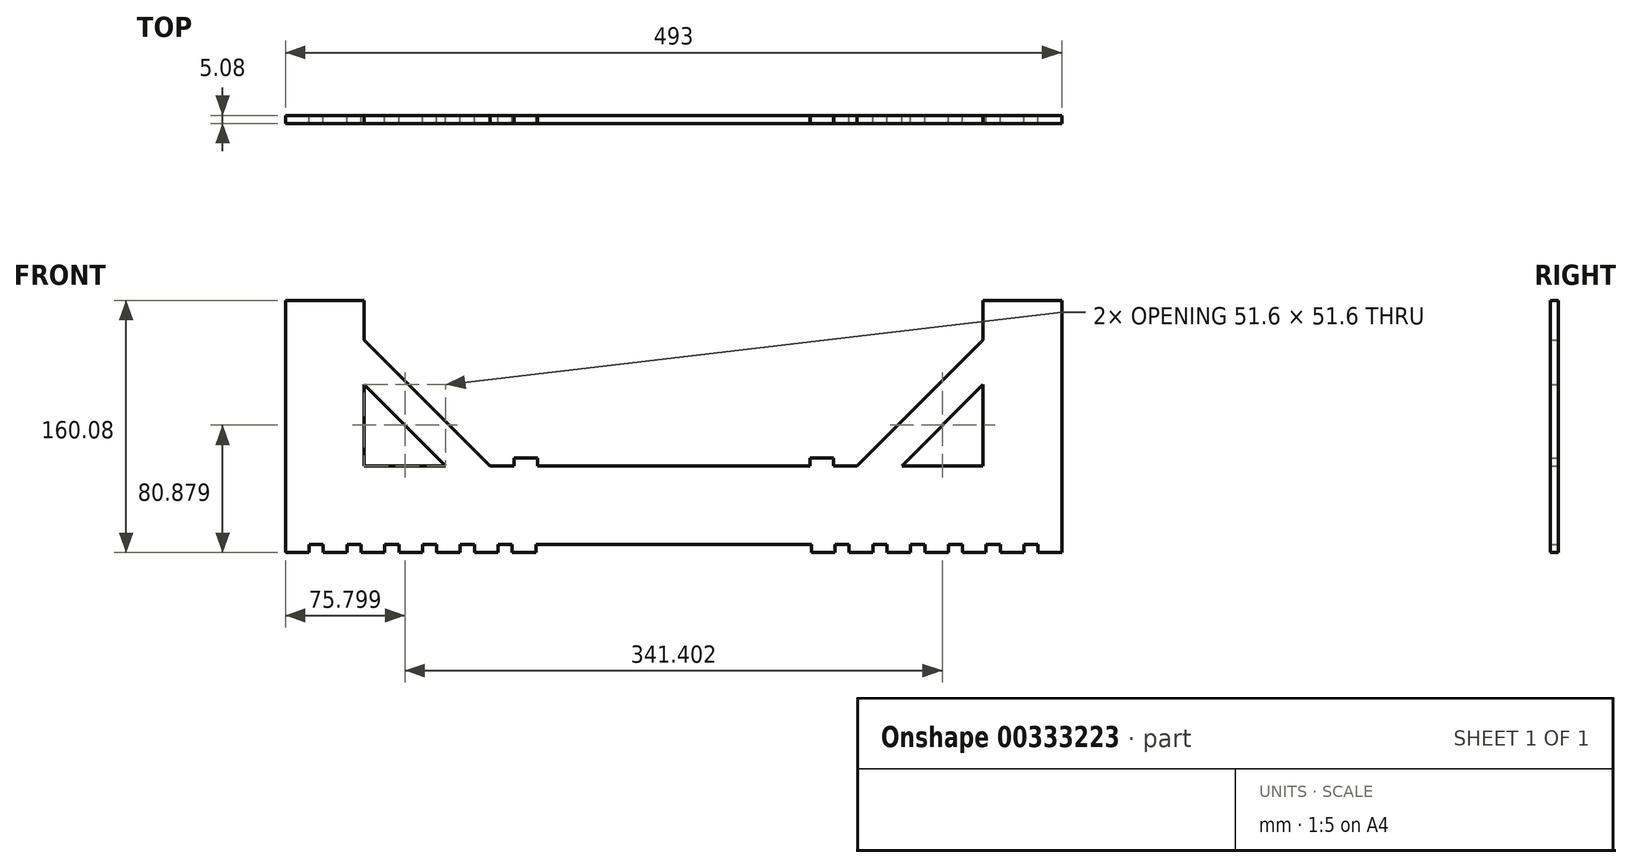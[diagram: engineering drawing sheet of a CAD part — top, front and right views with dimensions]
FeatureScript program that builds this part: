
annotation { "Feature Type Name" : "Feature", "Feature Type Description" : "" }
export const myFeature = defineFeature(function(context is Context, id is Id, definition is map)
    precondition{}
    {
        {
            var Q0;
            Q0=qCreatedBy(makeId("Front.planeOp"),FACE);
            var sketch = newSketch(context, id + "F0", { "sketchPlane" : qUnion([Q0])});
            skLineSegment(sketch, "E0", {"start": v(0, 0) * mm, "end": v(-246.5, 0) * mm});
            skLineSegment(sketch, "E1", {"start": v(-246.5, 0) * mm, "end": v(-246.5, 130) * mm});
            skLineSegment(sketch, "E2", {"start": v(-246.5, 130) * mm, "end": v(-196.5, 130) * mm});
            skLineSegment(sketch, "E3", {"start": v(-196.5, 130) * mm, "end": v(-196.5, 50) * mm});
            skLineSegment(sketch, "E4", {"start": v(-196.5, 50) * mm, "end": v(0, 50) * mm});
            skLineSegment(sketch, "E5", {"start": v(0, 50) * mm, "end": v(0, 0) * mm});
            skLineSegment(sketch, "E6", {"start": v(-196.5, 130) * mm, "end": v(-116.5, 50) * mm});
            skLineSegment(sketch, "E7", {"start": v(-196.5, 101.6) * mm, "end": v(-144.9, 50) * mm});
            skLineSegment(sketch, "E8", {"start": v(-246.5, 0) * mm, "end": v(-246.5, -5.08) * mm});
            skLineSegment(sketch, "E9", {"start": v(-246.5, -5.08) * mm, "end": v(-231.5, -5.08) * mm});
            skLineSegment(sketch, "E10", {"start": v(-231.5, -5.08) * mm, "end": v(-231.5, 0) * mm});
            skLineSegment(sketch, "E11.MirrorCS", {"start": v(196.5, 50) * mm, "end": v(0, 50) * mm});
            skLineSegment(sketch, "E12.MirrorCS", {"start": v(196.5, 130) * mm, "end": v(196.5, 50) * mm});
            skLineSegment(sketch, "E13.MirrorCS", {"start": v(196.5, 130) * mm, "end": v(116.5, 50) * mm});
            skLineSegment(sketch, "E14.MirrorCS", {"start": v(196.5, 101.6) * mm, "end": v(144.9, 50) * mm});
            skLineSegment(sketch, "E15.MirrorCS", {"start": v(246.5, 130) * mm, "end": v(196.5, 130) * mm});
            skLineSegment(sketch, "E16.MirrorCS", {"start": v(0, 0) * mm, "end": v(246.5, 0) * mm});
            skLineSegment(sketch, "E17.MirrorCS", {"start": v(246.5, 0) * mm, "end": v(246.5, 130) * mm});
            skLineSegment(sketch, "E18.1.0.0", {"start": v(-207.5, -5.08) * mm, "end": v(-207.5, 0) * mm});
            skLineSegment(sketch, "E18.1.0.1", {"start": v(-222.5, -5.08) * mm, "end": v(-207.5, -5.08) * mm});
            skLineSegment(sketch, "E18.1.0.2", {"start": v(-222.5, 0) * mm, "end": v(-222.5, -5.08) * mm});
            skLineSegment(sketch, "E18.2.0.0", {"start": v(-183.5, -5.08) * mm, "end": v(-183.5, 0) * mm});
            skLineSegment(sketch, "E18.2.0.1", {"start": v(-198.5, -5.08) * mm, "end": v(-183.5, -5.08) * mm});
            skLineSegment(sketch, "E18.2.0.2", {"start": v(-198.5, 0) * mm, "end": v(-198.5, -5.08) * mm});
            skLineSegment(sketch, "E18.3.0.0", {"start": v(-159.5, -5.08) * mm, "end": v(-159.5, 0) * mm});
            skLineSegment(sketch, "E18.3.0.1", {"start": v(-174.5, -5.08) * mm, "end": v(-159.5, -5.08) * mm});
            skLineSegment(sketch, "E18.3.0.2", {"start": v(-174.5, 0) * mm, "end": v(-174.5, -5.08) * mm});
            skLineSegment(sketch, "E18.4.0.0", {"start": v(-135.5, -5.08) * mm, "end": v(-135.5, 0) * mm});
            skLineSegment(sketch, "E18.4.0.1", {"start": v(-150.5, -5.08) * mm, "end": v(-135.5, -5.08) * mm});
            skLineSegment(sketch, "E18.4.0.2", {"start": v(-150.5, 0) * mm, "end": v(-150.5, -5.08) * mm});
            skLineSegment(sketch, "E18.5.0.0", {"start": v(-111.5, -5.08) * mm, "end": v(-111.5, 0) * mm});
            skLineSegment(sketch, "E18.5.0.1", {"start": v(-126.5, -5.08) * mm, "end": v(-111.5, -5.08) * mm});
            skLineSegment(sketch, "E18.5.0.2", {"start": v(-126.5, 0) * mm, "end": v(-126.5, -5.08) * mm});
            skLineSegment(sketch, "E18.6.0.0", {"start": v(-87.5, -5.08) * mm, "end": v(-87.5, 0) * mm});
            skLineSegment(sketch, "E18.6.0.1", {"start": v(-102.5, -5.08) * mm, "end": v(-87.5, -5.08) * mm});
            skLineSegment(sketch, "E18.6.0.2", {"start": v(-102.5, 0) * mm, "end": v(-102.5, -5.08) * mm});
            skLineSegment(sketch, "E18.direction1", {"start": v(-246.5, -5.08) * mm, "end": v(-222.5, -5.08) * mm, "construction": true});
            skLineSegment(sketch, "E19.MirrorCS", {"start": v(246.5, 0) * mm, "end": v(246.5, -5.08) * mm});
            skLineSegment(sketch, "E20.MirrorCS", {"start": v(231.5, -5.08) * mm, "end": v(231.5, 0) * mm});
            skLineSegment(sketch, "E21.MirrorCS", {"start": v(222.5, 0) * mm, "end": v(222.5, -5.08) * mm});
            skLineSegment(sketch, "E22.MirrorCS", {"start": v(222.5, -5.08) * mm, "end": v(207.5, -5.08) * mm});
            skLineSegment(sketch, "E23.MirrorCS", {"start": v(207.5, -5.08) * mm, "end": v(207.5, 0) * mm});
            skLineSegment(sketch, "E24.MirrorCS", {"start": v(198.5, 0) * mm, "end": v(198.5, -5.08) * mm});
            skLineSegment(sketch, "E25.MirrorCS", {"start": v(198.5, -5.08) * mm, "end": v(183.5, -5.08) * mm});
            skLineSegment(sketch, "E26.MirrorCS", {"start": v(183.5, -5.08) * mm, "end": v(183.5, 0) * mm});
            skLineSegment(sketch, "E27.MirrorCS", {"start": v(174.5, 0) * mm, "end": v(174.5, -5.08) * mm});
            skLineSegment(sketch, "E28.MirrorCS", {"start": v(174.5, -5.08) * mm, "end": v(159.5, -5.08) * mm});
            skLineSegment(sketch, "E29.MirrorCS", {"start": v(159.5, -5.08) * mm, "end": v(159.5, 0) * mm});
            skLineSegment(sketch, "E30.MirrorCS", {"start": v(150.5, 0) * mm, "end": v(150.5, -5.08) * mm});
            skLineSegment(sketch, "E31.MirrorCS", {"start": v(150.5, -5.08) * mm, "end": v(135.5, -5.08) * mm});
            skLineSegment(sketch, "E32.MirrorCS", {"start": v(135.5, -5.08) * mm, "end": v(135.5, 0) * mm});
            skLineSegment(sketch, "E33.MirrorCS", {"start": v(87.5, -5.08) * mm, "end": v(87.5, 0) * mm});
            skLineSegment(sketch, "E34.MirrorCS", {"start": v(102.5, -5.08) * mm, "end": v(87.5, -5.08) * mm});
            skLineSegment(sketch, "E35.MirrorCS", {"start": v(102.5, 0) * mm, "end": v(102.5, -5.08) * mm});
            skLineSegment(sketch, "E36.MirrorCS", {"start": v(111.5, -5.08) * mm, "end": v(111.5, 0) * mm});
            skLineSegment(sketch, "E37.MirrorCS", {"start": v(126.5, 0) * mm, "end": v(126.5, -5.08) * mm});
            skLineSegment(sketch, "E38.MirrorCS", {"start": v(126.5, -5.08) * mm, "end": v(111.5, -5.08) * mm});
            skLineSegment(sketch, "E39", {"start": v(231.5, -5.08) * mm, "end": v(246.5, -5.08) * mm});
            skSolve(sketch);
        }
        {
            var Q0;
            Q0=qSketchRegion(id+"F0",true);
            extrude(context, id + "F1", {"entities" : qUnion([Q0]), "depth" : 5.08 * mm});
        }
        {
            var Q0;
            Q0=makeQuery(id+"F1.opExtrude","SWEPT_FACE",FACE,{"disambiguationData":[OSD([sQuery(id+"F0.wireOp",EDGE,"E2")])]});
            var Q1;
            Q1=makeQuery(id+"F1.opExtrude","SWEPT_FACE",FACE,{"disambiguationData":[OSD([sQuery(id+"F0.wireOp",EDGE,"E15.MirrorCS")])]});
            extrude(context, id + "F2", {"entities" : qUnion([Q0, Q1]), "operationType" : NewBodyOperationType.ADD, "depth" : 25 * mm});
        }
        {
            var Q0;
            Q0=makeQuery(id+"F1.opExtrude","SWEPT_FACE",FACE,{"disambiguationData":[OSD([sQuery(id+"F0.wireOp",EDGE,"E4"),sQuery(id+"F0.wireOp",EDGE,"E11.MirrorCS")])]});
            var sketch = newSketch(context, id + "F3", { "sketchPlane" : qUnion([Q0])});
            skLineSegment(sketch, "E40.bottom", {"start": v(101.5, -5.08) * mm, "end": v(86.5, -5.08) * mm});
            skLineSegment(sketch, "E40.top", {"start": v(101.5, 0) * mm, "end": v(86.5, 0) * mm});
            skLineSegment(sketch, "E40.right", {"start": v(86.5, -5.08) * mm, "end": v(86.5, 0) * mm});
            skLineSegment(sketch, "E41", {"start": v(101.5, -5.08) * mm, "end": v(101.5, 0) * mm});
            skPoint(sketch, "E40.left.start.orphan", {"position": v(116.5, -5.08) * mm});
            skPoint(sketch, "E42.orphan", {"position": v(116.5, 0) * mm});
            skSolve(sketch);
        }
        {
            var Q0;
            Q0=qSketchRegion(id+"F3",true);
            extrude(context, id + "F4", {"entities" : qUnion([Q0]), "operationType" : NewBodyOperationType.ADD, "depth" : 5.08 * mm});
        }
        {
            var Q0;
            {var subQ1=sQuery(id+"F0.wireOp",EDGE,"E6");var subQ47=sQuery(id+"F0.wireOp",EDGE,"E11.MirrorCS");var subQ52=sQuery(id+"F0.wireOp",EDGE,"E4");Q0=makeQuery(id+"F4.boolean.opBoolean","SPLIT",FACE,{"disambiguationData":[TD([makeQuery(id+"F1.opExtrude","SWEPT_FACE",FACE,{"disambiguationData":[OSD([subQ1])]})])],"derivedFrom":makeQuery(id+"F1.opExtrude","SWEPT_FACE",FACE,{"disambiguationData":[OSD([subQ52,subQ47])]})});}
            var sketch = newSketch(context, id + "F5", { "sketchPlane" : qUnion([Q0])});
            skLineSegment(sketch, "E43.bottom", {"start": v(-101.5, -5.08) * mm, "end": v(-86.5, -5.08) * mm});
            skLineSegment(sketch, "E43.top", {"start": v(-101.5, 0) * mm, "end": v(-86.5, 0) * mm});
            skLineSegment(sketch, "E43.right", {"start": v(-86.5, -5.08) * mm, "end": v(-86.5, 0) * mm});
            skLineSegment(sketch, "E44", {"start": v(-101.5, -5.08) * mm, "end": v(-101.5, 0) * mm});
            skPoint(sketch, "E43.left.start.orphan", {"position": v(-116.5, -5.08) * mm});
            skPoint(sketch, "E45.orphan", {"position": v(-116.5, 0) * mm});
            skSolve(sketch);
        }
        {
            var Q0;
            Q0=qSketchRegion(id+"F5",true);
            extrude(context, id + "F6", {"entities" : qUnion([Q0]), "operationType" : NewBodyOperationType.ADD, "depth" : 5.08 * mm});
        }
    });
